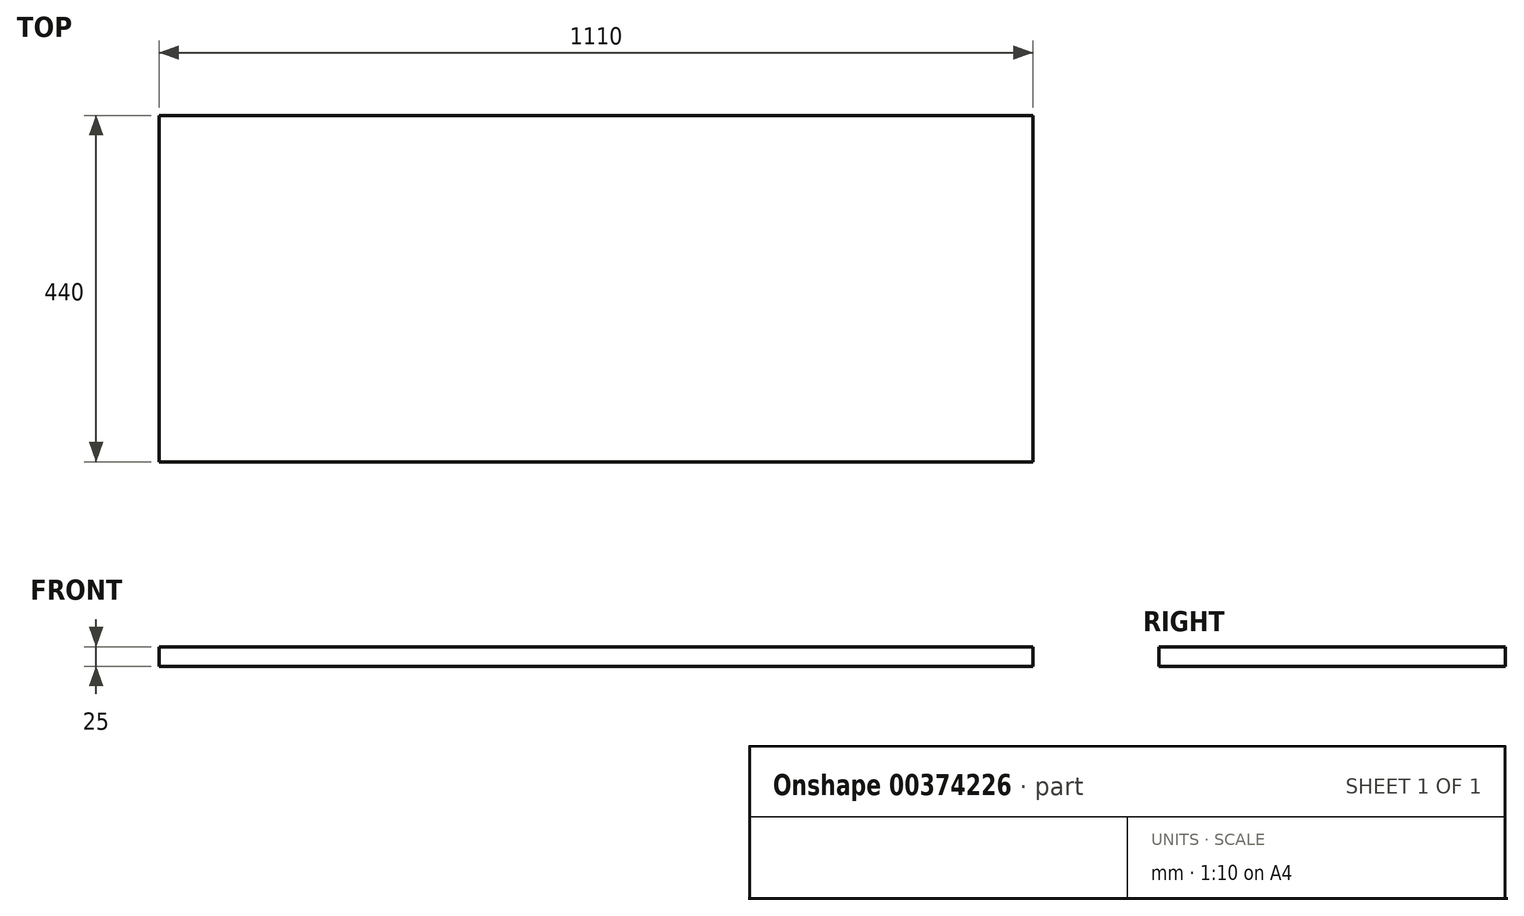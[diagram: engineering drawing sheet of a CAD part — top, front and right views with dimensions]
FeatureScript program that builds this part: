
annotation { "Feature Type Name" : "Feature", "Feature Type Description" : "" }
export const myFeature = defineFeature(function(context is Context, id is Id, definition is map)
    precondition{}
    {
        {
            var Q0;
            Q0=qCreatedBy(makeId("Top.planeOp"),FACE);
            var sketch = newSketch(context, id + "F0", { "sketchPlane" : qUnion([Q0])});
            skLineSegment(sketch, "E0.bottom", {"start": v(555, 220) * mm, "end": v(-555, 220) * mm});
            skLineSegment(sketch, "E0.top", {"start": v(555, -220) * mm, "end": v(-555, -220) * mm});
            skLineSegment(sketch, "E0.left", {"start": v(555, 220) * mm, "end": v(555, -220) * mm});
            skLineSegment(sketch, "E0.right", {"start": v(-555, 220) * mm, "end": v(-555, -220) * mm});
            skPoint(sketch, "E0.middle", {"position": v(0, 0) * mm});
            skSolve(sketch);
        }
        {
            var Q0;
            Q0=makeQuery(id+"F0.imprint","IMPRINT",FACE,{"disambiguationData":[TD([[makeQuery(id+"F0.imprint","IMPRINT",EDGE,{"derivedFrom":sQuery(id+"F0.wireOp",EDGE,"E0.bottom")}),1.0]])]});
            extrude(context, id + "F1", {"entities" : qUnion([Q0]), "depth" : -25 * mm});
        }
    });
